# Revit family: Faucet-Lavatory-KOHLER-July-K-16312BR_1
name_source: partatom
category: Plumbing Fixtures
units: mm (PartAtom-declared; Revit-internal decimal feet)

## family parameters
Cut with Voids When Loaded = No
Host = Face
OmniClass Number = 23.31.11.00
OmniClass Title = Faucets
Part Type = Normal
Room Calculation Point = No
Round Connector Dimension = Use Diameter
Shared = No

## types (3) — shared parameters
ADA Compliant = No
Assembly Code = D2010
CW Connection = Yes
Cold Water Inlet = Cold Water Inlet
Date Modified = 09/21/2022
Default Elevation = 36"
Description = Pillar Lavatory Faucet
Drain Included = No
Flow Rate = 10 GPM
HW Connection = No
Handle Clearance = 2 11/16"
Height = 4 9/16"
Hot Water Inlet = Hot Water Inlet
Length = 3 3/16"
Manufacturer = Kohler Co.
Master Format 2014 = 22 41 39
Master Format 2014 Name = Residential Faucets, Supplies, and Trim
Material = Premium Metal Construction
Pressure = 43.50 psi
Product Name = July
Spout Reach = 3 3/16"
URL = https://br.kohler.com
Vent Connection = No
Waste Connection = No
Waste Water Outlet = Waste Water Outlet
WaterSense Certified = No
Width = 1 15/16"

## per-type parameters (varying)
| type | Finish | Model | Type |
| 4ND, CP-Polished Chrome | Kohler-Metal-CP-Polished_Chrome | K-16312BR-4ND-CP | 1 |
| 4, CP-Polished Chrome | Kohler-Metal-CP-Polished_Chrome | K-16312BR-4-CP | 2 |
| 4, 0-White | Kohler-Metal-0-White | K-16312BR-4-0 | 3 |

## geometry (parser evidence)
native form markers: Sweep x6
no freeform markers — native parametric forms only
